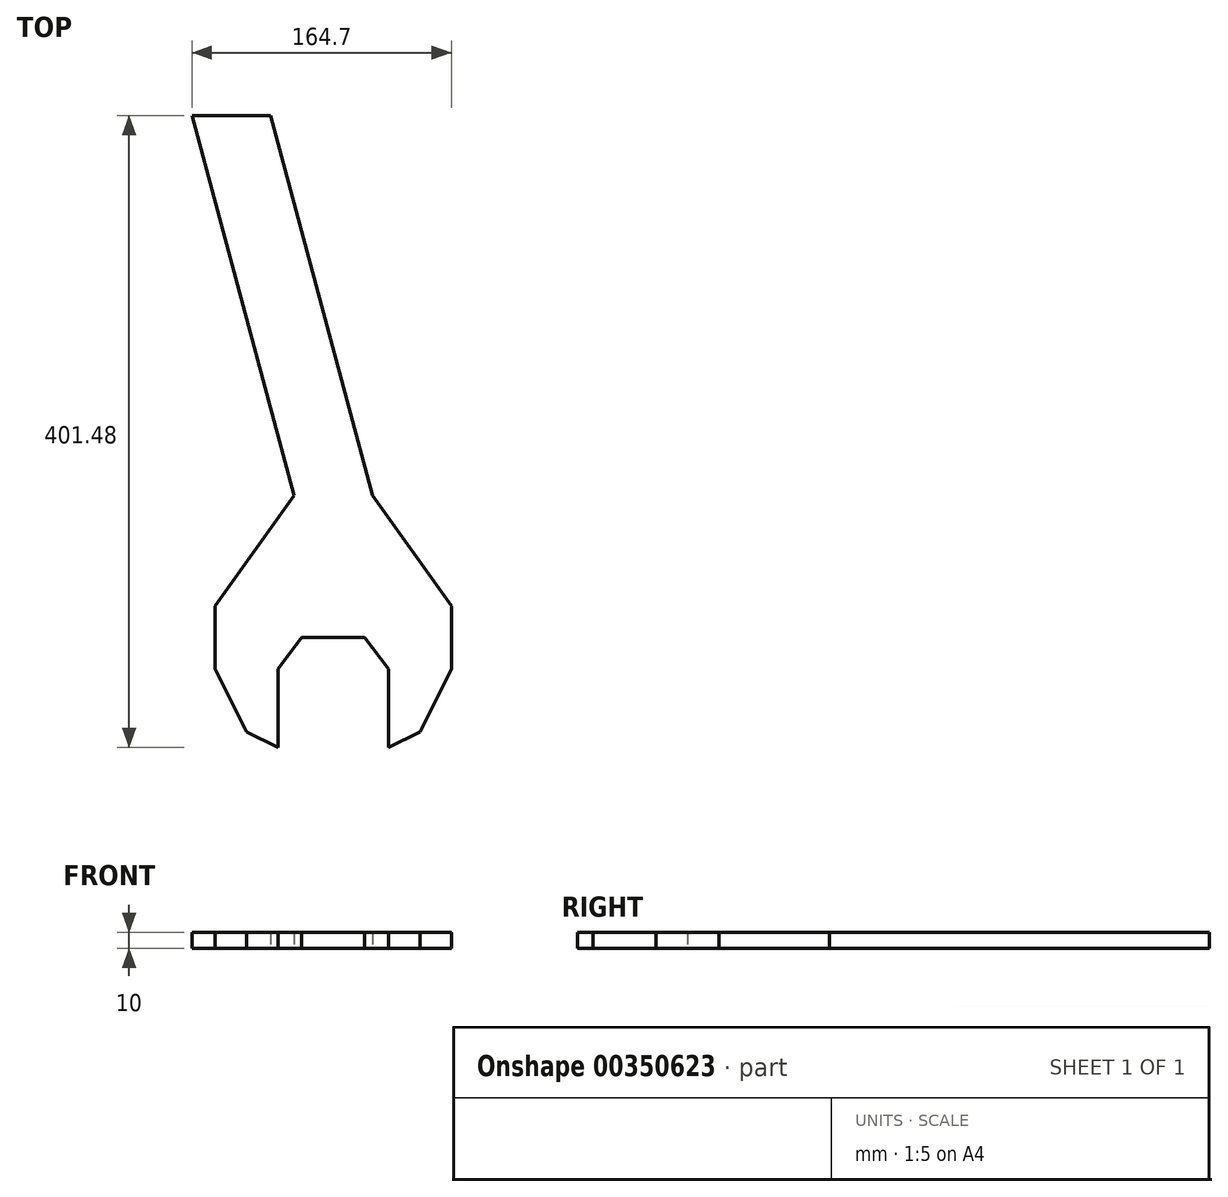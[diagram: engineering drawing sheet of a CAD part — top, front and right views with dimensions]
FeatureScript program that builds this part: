
annotation { "Feature Type Name" : "Feature", "Feature Type Description" : "" }
export const myFeature = defineFeature(function(context is Context, id is Id, definition is map)
    precondition{}
    {
        {
            var Q0;
            Q0=qCreatedBy(makeId("Top.planeOp"),FACE);
            var sketch = newSketch(context, id + "F0", { "sketchPlane" : qUnion([Q0])});
            skLineSegment(sketch, "E0", {"start": v(-20, 0) * mm, "end": v(20, 0) * mm});
            skLineSegment(sketch, "E1", {"start": v(-20, 0) * mm, "end": v(-35, -20) * mm});
            skLineSegment(sketch, "E2", {"start": v(-35, -20) * mm, "end": v(-35, -70) * mm});
            skLineSegment(sketch, "E3", {"start": v(0, 0) * mm, "end": v(0, -67.64) * mm, "construction": true});
            skLineSegment(sketch, "E4.MirrorCS", {"start": v(20, 0) * mm, "end": v(35, -20) * mm});
            skLineSegment(sketch, "E5.MirrorCS", {"start": v(35, -20) * mm, "end": v(35, -70) * mm});
            skLineSegment(sketch, "E6", {"start": v(-35, -70) * mm, "end": v(-55, -60) * mm});
            skLineSegment(sketch, "E7", {"start": v(-55, -60) * mm, "end": v(-75, -20) * mm});
            skLineSegment(sketch, "E8", {"start": v(-75, -20) * mm, "end": v(-75, 20) * mm});
            skLineSegment(sketch, "E9", {"start": v(-75, 20) * mm, "end": v(-25, 90) * mm});
            skLineSegment(sketch, "E10.MirrorCS", {"start": v(35, -70) * mm, "end": v(55, -60) * mm});
            skLineSegment(sketch, "E11.MirrorCS", {"start": v(55, -60) * mm, "end": v(75, -20) * mm});
            skLineSegment(sketch, "E12.MirrorCS", {"start": v(75, 20) * mm, "end": v(25, 90) * mm});
            skLineSegment(sketch, "E13.MirrorCS", {"start": v(75, -20) * mm, "end": v(75, 20) * mm});
            skLineSegment(sketch, "E14", {"start": v(-25, 90) * mm, "end": v(-89.7, 331.48) * mm});
            skLineSegment(sketch, "E15", {"start": v(-89.7, 331.48) * mm, "end": v(-39.7, 331.48) * mm});
            skLineSegment(sketch, "E16", {"start": v(-39.7, 331.48) * mm, "end": v(25, 90) * mm});
            skLineSegment(sketch, "E17", {"start": v(25, 90) * mm, "end": v(157.59, 90) * mm, "construction": true});
            skSolve(sketch);
        }
        {
            var Q0;
            Q0=makeQuery(id+"F0.imprint","IMPRINT",FACE,{"disambiguationData":[TD([[makeQuery(id+"F0.imprint","IMPRINT",EDGE,{"derivedFrom":sQuery(id+"F0.wireOp",EDGE,"E0")}),1.0]])]});
            extrude(context, id + "F1", {"entities" : qUnion([Q0]), "depth" : 10 * mm});
        }
    });
